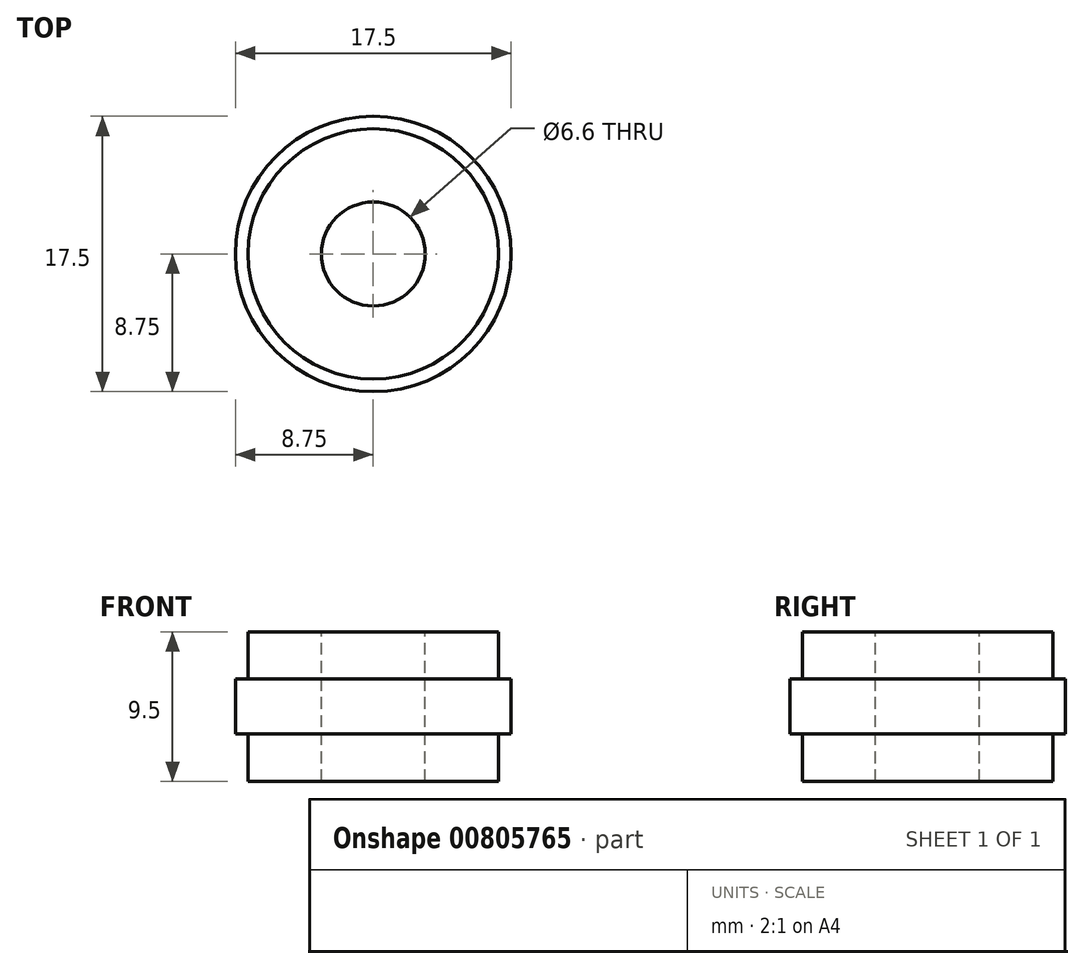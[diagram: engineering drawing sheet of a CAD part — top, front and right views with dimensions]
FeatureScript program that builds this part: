
annotation { "Feature Type Name" : "Feature", "Feature Type Description" : "" }
export const myFeature = defineFeature(function(context is Context, id is Id, definition is map)
    precondition{}
    {
        {
            var Q0;
            Q0=qCreatedBy(makeId("Top.planeOp"),FACE);
            var sketch = newSketch(context, id + "F0", { "sketchPlane" : qUnion([Q0])});
            skCircle(sketch, "E0", {"center": v(0, 0) * mm, "radius": 7.95 * mm});
            skSolve(sketch);
        }
        {
            var Q0;
            Q0=qSketchRegion(id+"F0",true);
            extrude(context, id + "F1", {"entities" : qUnion([Q0]), "depth" : 3 * mm});
        }
        {
            var Q0;
            Q0=makeQuery(id+"F1.opExtrude","CAP_FACE",FACE,{"disambiguationData":[OSD([sQuery(id+"F0.wireOp",EDGE,"E0")])],"isStart":true});
            var sketch = newSketch(context, id + "F2", { "sketchPlane" : qUnion([Q0])});
            skCircle(sketch, "E1", {"center": v(0, 0) * mm, "radius": 8.75 * mm});
            skSolve(sketch);
        }
        {
            var Q0;
            Q0=qSketchRegion(id+"F2",true);
            extrude(context, id + "F3", {"entities" : qUnion([Q0]), "operationType" : NewBodyOperationType.ADD, "depth" : 3.5 * mm});
        }
        {
            var Q0;
            Q0=makeQuery(id+"F3.opExtrude","CAP_FACE",FACE,{"disambiguationData":[OSD([sQuery(id+"F2.wireOp",EDGE,"E1")])],"isStart":false});
            var sketch = newSketch(context, id + "F4", { "sketchPlane" : qUnion([Q0])});
            skCircle(sketch, "E2", {"center": v(0, 0) * mm, "radius": 7.95 * mm});
            skSolve(sketch);
        }
        {
            var Q0;
            Q0=qSketchRegion(id+"F4",true);
            extrude(context, id + "F5", {"entities" : qUnion([Q0]), "operationType" : NewBodyOperationType.ADD, "depth" : 3 * mm});
        }
        {
            var Q0;
            Q0=makeQuery(id+"F1.opExtrude","CAP_FACE",FACE,{"disambiguationData":[OSD([sQuery(id+"F0.wireOp",EDGE,"E0")])],"isStart":false});
            var sketch = newSketch(context, id + "F6", { "sketchPlane" : qUnion([Q0])});
            skCircle(sketch, "E3", {"center": v(0, 0) * mm, "radius": 3 * mm});
            skCircle(sketch, "E4", {"center": v(0, 0) * mm, "radius": 1.05 * mm});
            skSolve(sketch);
        }
        {
            var Q0;
            Q0=sQuery(id+"F6.wireOp",VERTEX,"E3.center");
            var Q1;
            Q1=makeQuery(id+"F1.opExtrude","SWEPT_BODY",BODY,{"disambiguationData":[OSD([sQuery(id+"F0.wireOp",EDGE,"E0")])]});
            hole(context, id + "F7", {"style" : HoleStyle.SIMPLE, "endStyle" : HoleEndStyle.THROUGH, "standardTappedOrClearance" : lookupTablePath({ "standard" : "ISO", "fit" : "Normal", "size" : "M6", "type" : "Clearance" }), "standardBlindInLast" : lookupTablePath({ "fit" : "Standard", "standard" : "ISO", "size" : "M6", "type" : "Clearance" }), "holeDiameter" : 6.6 * mm, "majorDiameter" : 5 * mm, "isTappedThrough" : true, "tappedDepth" : 12 * mm, "tapClearance" : 3, "locations" : qUnion([Q0]), "scope" : qUnion([Q1])});
        }
    });
